# Revit family: LK4409BF
name_source: partatom
category: Plumbing Fixtures
units: mm (PartAtom-declared; Revit-internal decimal feet)

## family parameters
Cut with Voids When Loaded = No
Host = Face
Part Type = Normal
Room Calculation Point = No
Round Connector Dimension = Use Diameter
Shared = No

## types (12) — shared parameters
ACTIVATION BY = MECHANICAL BOTTLE FILLER BUTTON WITH MECHANICAL FRONT BUBBLER BUTTON
APPROX. SHIPPING WEIGHT = 203
BUBBLER STYLE = VANDAL RESISTANT
CHILLING OPTION = NON REFRIGERATED
CW Connection = No
DIMENSIONS (LxWxH) = 21-1/4" x 32-7/8" x 38-7/16"
Default Elevation = 3' - 2 3/4"
HW Connection = No
INSTALLATION LOCATION = OOUTDOOR
MOUNTING TYPE = WALL MOUNT
NO OF STATIONS SERVED = 3
POWER = NO ELECTRIC REQUIRED
SPECIAL FEATURES = 316 STAINLESS, LAMINAR FLOW, HEAVY DUTY VANDAL RESISTANT
Vent Connection = No
Waste Connection = No

## per-type parameters (varying)
| type | BGE | BLK | BLU | BRN | EVG | FINISH | GRY | ORN | PUR | RED | TER | WHT | YLW |
| WHT | No | No | No | No | No | White (WHT) | No | No | No | No | No | Yes | No |
| EVG | No | No | No | No | Yes | Evergreen (EVG)
Yellow (YLW) | No | No | No | No | No | No | No |
| BLU | No | No | Yes | No | No | Blue (BLU)
Yellow (YLW) | No | No | No | No | No | No | No |
| PUR | No | No | No | No | No | Purple (PUR) | No | No | Yes | No | No | No | No |
| RED | No | No | No | No | No | Red (RED) | No | No | No | Yes | No | No | No |
| TER | No | No | No | No | No | Terracotta (TER) | No | No | No | No | Yes | No | No |
| ORN | No | No | No | No | No | Orange (ORN) | No | Yes | No | No | No | No | No |
| YLW | No | No | No | No | No | Yellow (YLW) | No | No | No | No | No | No | Yes |
| BLK | No | Yes | No | No | No | Black (BLK) | No | No | No | No | No | No | No |
| GRY | No | No | No | No | No | Gray (GRY) | Yes | No | No | No | No | No | No |
| BRN | No | No | No | Yes | No | Brown (BRN) | No | No | No | No | No | No | No |
| BGE | Yes | No | No | No | No | Beige (BGE) | No | No | No | No | No | No | No |

## geometry (parser evidence)
native form markers: Blend x2, Sweep x3
no freeform markers — native parametric forms only
